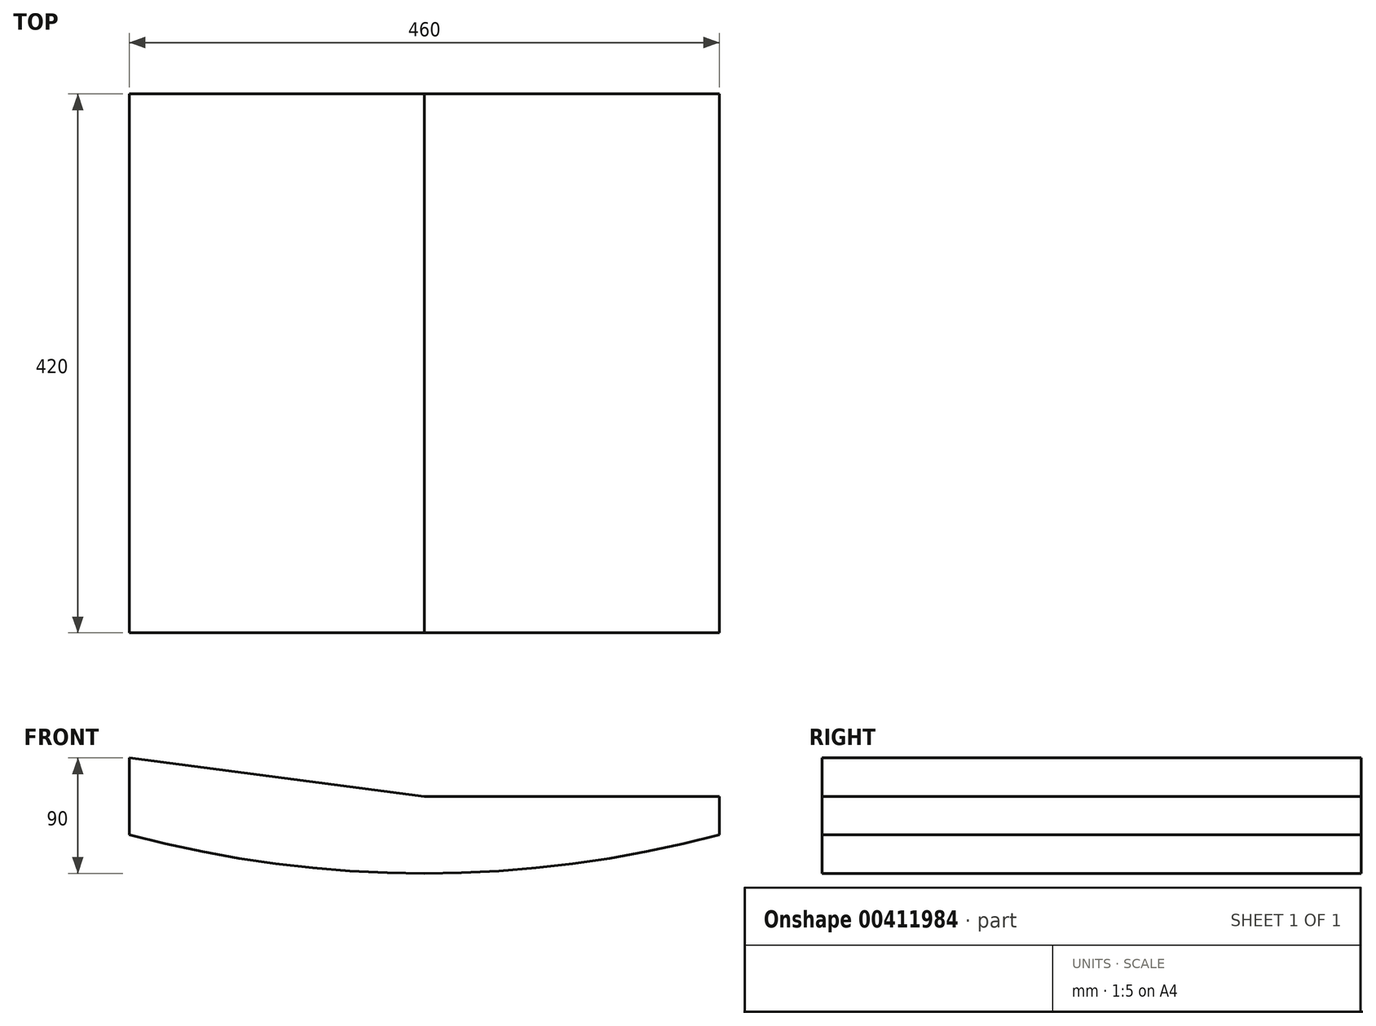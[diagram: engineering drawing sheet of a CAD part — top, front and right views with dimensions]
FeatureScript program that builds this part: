
annotation { "Feature Type Name" : "Feature", "Feature Type Description" : "" }
export const myFeature = defineFeature(function(context is Context, id is Id, definition is map)
    precondition{}
    {
        {
            var Q0;
            Q0=qCreatedBy(makeId("Front.planeOp"),FACE);
            var sketch = newSketch(context, id + "F0", { "sketchPlane" : qUnion([Q0])});
            skLineSegment(sketch, "E0.bottom", {"start": v(230, -30) * mm, "end": v(-230, -30) * mm});
            skLineSegment(sketch, "E0.left", {"start": v(230, -30) * mm, "end": v(230, 0) * mm});
            skLineSegment(sketch, "E0.right", {"start": v(-230, -30) * mm, "end": v(-230, 30) * mm});
            skPoint(sketch, "E0.middle", {"position": v(0, 0) * mm});
            skLineSegment(sketch, "E1", {"start": v(-230, 0) * mm, "end": v(0, -30) * mm});
            skLineSegment(sketch, "E2", {"start": v(230, 0) * mm, "end": v(0, 0) * mm});
            skLineSegment(sketch, "E3", {"start": v(-230, 30) * mm, "end": v(0, 0) * mm});
            skPoint(sketch, "E4.orphan", {"position": v(230, 30) * mm});
            skArc(sketch, "E5", {"start": v(-230, -30) * mm, "mid": v(0, -60) * mm, "end": v(230, -30) * mm});
            skSolve(sketch);
        }
        {
            var Q0;
            {var subQ3=sQuery(id+"F0.wireOp",EDGE,"E1");Q0=makeQuery(id+"F0.imprint","IMPRINT",FACE,{"disambiguationData":[TD([[makeQuery(id+"F0.imprint","IMPRINT",EDGE,{"derivedFrom":subQ3}),-1.0]])]});}
            var Q1;
            {var subQ3=sQuery(id+"F0.wireOp",EDGE,"E0.left");Q1=makeQuery(id+"F0.imprint","IMPRINT",FACE,{"disambiguationData":[TD([[makeQuery(id+"F0.imprint","IMPRINT",EDGE,{"derivedFrom":subQ3}),1.0]])]});}
            var Q2;
            {var subQ0=sQuery(id+"F0.wireOp",EDGE,"qFTBzpEx-4129-z8Y8-YS7b-F00NVrmki1eQ");Q2=makeQuery(id+"F0.imprint","IMPRINT",FACE,{"disambiguationData":[TD([[makeQuery(id+"F0.imprint","IMPRINT",EDGE,{"derivedFrom":subQ0}),1.0]])]});}
            var Q3;
            {var subQ0=sQuery(id+"F0.wireOp",EDGE,"E5");Q3=makeQuery(id+"F0.imprint","IMPRINT",FACE,{"disambiguationData":[TD([[makeQuery(id+"F0.imprint","IMPRINT",EDGE,{"derivedFrom":subQ0}),1.0]])]});}
            extrude(context, id + "F1", {"entities" : qUnion([Q0, Q1, Q2, Q3]), "oppositeDirection" : true, "depth" : 420 * mm});
        }
    });
